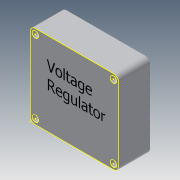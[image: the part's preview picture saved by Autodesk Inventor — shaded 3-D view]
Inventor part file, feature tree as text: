
AUTODESK INVENTOR PART (.ipt)
format: ipt  version: 2014 (Build 180170000, 170)  size: 97,280 bytes
history: native  units: in
note: dims shown in document units (in); Inventor stores cm internally (conversion verified against a paired STEP export)
features: sketch x2, extrude x1
ambient origin geometry x8: Origin, YZ Plane, XZ Plane, XY Plane, X Axis, Y Axis, Z Axis, Center Point
bodies: Solid1 (feature_tree)
feature tree (3):
  extrude  "Extrusion1"  Depth=2.0in
  sketch  "Sketch2"  dims[d2=0.125in d3=0.156in d4=0.75in d5=0.0in]
  sketch  "Sketch1"  dims[d0=2.125in d1=2.0in]
